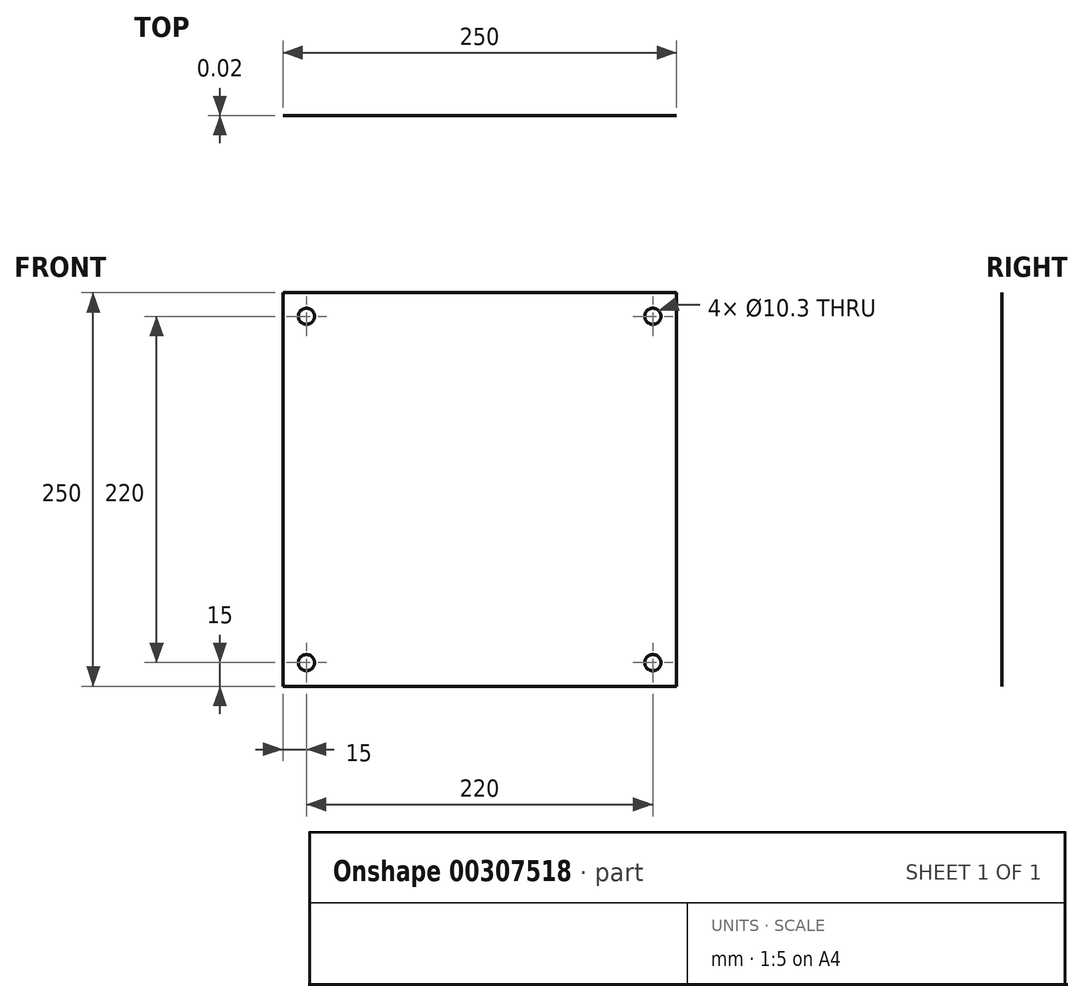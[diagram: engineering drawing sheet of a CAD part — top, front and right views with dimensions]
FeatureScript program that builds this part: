
annotation { "Feature Type Name" : "Feature", "Feature Type Description" : "" }
export const myFeature = defineFeature(function(context is Context, id is Id, definition is map)
    precondition{}
    {
        {
            var Q0;
            Q0=qCreatedBy(makeId("Front.planeOp"),FACE);
            var sketch = newSketch(context, id + "F0", { "sketchPlane" : qUnion([Q0])});
            skLineSegment(sketch, "E0.bottom", {"start": v(-125, 125) * mm, "end": v(125, 125) * mm});
            skLineSegment(sketch, "E0.top", {"start": v(-125, -125) * mm, "end": v(125, -125) * mm});
            skLineSegment(sketch, "E0.left", {"start": v(-125, 125) * mm, "end": v(-125, -125) * mm});
            skLineSegment(sketch, "E0.right", {"start": v(125, 125) * mm, "end": v(125, -125) * mm});
            skPoint(sketch, "E0.middle", {"position": v(0, 0) * mm});
            skPoint(sketch, "E1", {"position": v(-110, -110) * mm});
            skPoint(sketch, "E2", {"position": v(110, -110) * mm});
            skPoint(sketch, "E3", {"position": v(110, 110) * mm});
            skPoint(sketch, "E4", {"position": v(-110, 110) * mm});
            skSolve(sketch);
        }
        {
            var Q0;
            Q0 = qSketchRegion(id + "F0", true);
            extrude(context, id + "F1", {"entities" : qUnion([Q0]), "depth" : 1 / 50.8 * mm});
        }
        {
            var Q0;
            Q0=sQuery(id+"F0.wireOp",VERTEX,"E4");
            var Q1;
            Q1=sQuery(id+"F0.wireOp",VERTEX,"E1");
            var Q2;
            Q2=sQuery(id+"F0.wireOp",VERTEX,"E2");
            var Q3;
            Q3=sQuery(id+"F0.wireOp",VERTEX,"E3");
            var Q4;
            Q4=makeQuery(id+"F1.opExtrude","SWEPT_BODY",BODY,{"disambiguationData":[OSD([sQuery(id+"F0.wireOp",EDGE,"E0.bottom"),sQuery(id+"F0.wireOp",EDGE,"E0.top"),sQuery(id+"F0.wireOp",EDGE,"E0.left"),sQuery(id+"F0.wireOp",EDGE,"E0.right")])]});
            hole(context, id + "F2", {"style" : HoleStyle.SIMPLE, "endStyle" : HoleEndStyle.THROUGH, "oppositeDirection" : true, "standardTappedOrClearance" : lookupTablePath({ "standard" : "ISO", "engagement" : "75%", "pitch" : "1.75 mm", "size" : "M12", "type" : "Tapped" }), "standardBlindInLast" : lookupTablePath({ "standard" : "ISO", "engagement" : "75%", "pitch" : "1.75 mm", "size" : "M12", "type" : "Tapped" }), "holeDiameter" : 10.3 * mm, "showTappedDepth" : true, "tappedDepth" : 25.4 * mm, "tapClearance" : 3, "locations" : qUnion([Q0, Q1, Q2, Q3]), "scope" : qUnion([Q4]), "majorDiameter" : 12 * mm});
        }
    });
